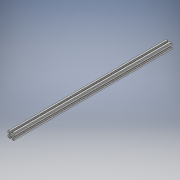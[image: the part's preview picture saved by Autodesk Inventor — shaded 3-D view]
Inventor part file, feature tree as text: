
AUTODESK INVENTOR PART (.ipt)
format: ipt  version: 2017 (Build 210142000, 142)  size: 252,416 bytes
history: native  units: in
note: dims shown in document units (in); Inventor stores cm internally (conversion verified against a paired STEP export)
features: extrude x1, sketch x1, fillet x1
ambient origin geometry x8: Origin, YZ Plane, XZ Plane, XY Plane, X Axis, Y Axis, Z Axis, Center Point
bodies: Solid1 (feature_tree)
feature tree (3):
  extrude  "Extrusion1"  [1 undecoded]
  sketch  "Sketch1"  dims[d0=25.3701in d1=0.0in]
  fillet  "Fillet6"  [1 undecoded]
note: 2 required parameter values undecoded (feature->parameter linkage not recoverable at this tier; creation-order binding heuristic only, values carry confidence <= 0.55)
